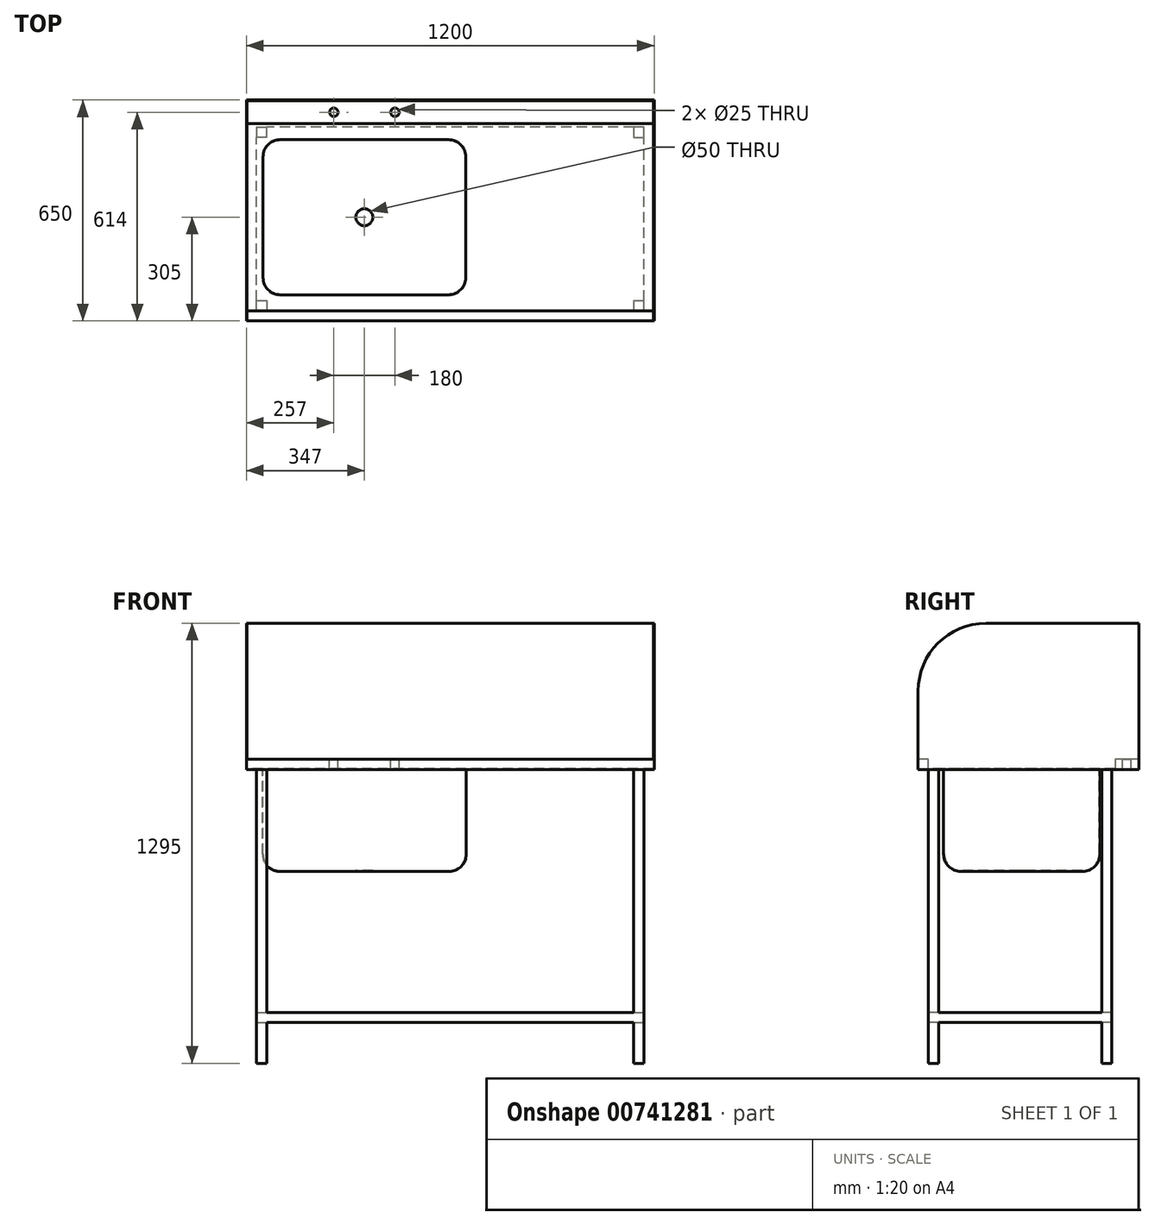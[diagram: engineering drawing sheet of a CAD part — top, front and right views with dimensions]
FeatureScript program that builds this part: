
annotation { "Feature Type Name" : "Feature", "Feature Type Description" : "" }
export const myFeature = defineFeature(function(context is Context, id is Id, definition is map)
    precondition{}
    {
        {
            var Q0;
            Q0=qCreatedBy(makeId("Right.planeOp"),FACE);
            var sketch = newSketch(context, id + "F0", { "sketchPlane" : qUnion([Q0])});
            skLineSegment(sketch, "E0", {"start": v(0, 0) * mm, "end": v(0, -30) * mm});
            skLineSegment(sketch, "E1", {"start": v(0, -30) * mm, "end": v(650, -30) * mm});
            skLineSegment(sketch, "E2", {"start": v(650, -30) * mm, "end": v(650, 400) * mm});
            skLineSegment(sketch, "E3", {"start": v(650, 400) * mm, "end": v(648, 400) * mm});
            skLineSegment(sketch, "E4", {"start": v(648, 400) * mm, "end": v(648, 0) * mm});
            skLineSegment(sketch, "E5", {"start": v(648, 0) * mm, "end": v(580, 0) * mm});
            skLineSegment(sketch, "E6", {"start": v(580, 0) * mm, "end": v(580, -28) * mm});
            skLineSegment(sketch, "E7", {"start": v(580, -28) * mm, "end": v(30, -28) * mm});
            skLineSegment(sketch, "E8", {"start": v(30, -28) * mm, "end": v(30, 0) * mm});
            skLineSegment(sketch, "E9", {"start": v(30, 0) * mm, "end": v(0, 0) * mm});
            skSolve(sketch);
        }
        {
            var Q0;
            Q0 = qSketchRegion(id + "F0", true);
            extrude(context, id + "F1", {"entities" : qUnion([Q0]), "depth" : 1200 * mm, "offsetDistance" : 25 * mm});
        }
        {
            var Q0;
            Q0=qCreatedBy(makeId("Front.planeOp"),FACE);
            var sketch = newSketch(context, id + "F2", { "sketchPlane" : qUnion([Q0])});
            skLineSegment(sketch, "E10.bottom", {"start": v(0, -30) * mm, "end": v(2, -30) * mm});
            skLineSegment(sketch, "E10.top", {"start": v(0, 400) * mm, "end": v(2, 400) * mm});
            skLineSegment(sketch, "E10.left", {"start": v(0, -30) * mm, "end": v(0, 400) * mm});
            skLineSegment(sketch, "E10.right", {"start": v(2, -30) * mm, "end": v(2, 400) * mm});
            skLineSegment(sketch, "E11.bottom", {"start": v(1200, -30) * mm, "end": v(1198, -30) * mm});
            skLineSegment(sketch, "E11.top", {"start": v(1200, 400) * mm, "end": v(1198, 400) * mm});
            skLineSegment(sketch, "E11.left", {"start": v(1200, -30) * mm, "end": v(1200, 400) * mm});
            skLineSegment(sketch, "E11.right", {"start": v(1198, -30) * mm, "end": v(1198, 400) * mm});
            skSolve(sketch);
        }
        {
            var Q0;
            Q0 = qSketchRegion(id + "F2", true);
            var Q1;
            Q1=makeQuery(id+"F1.opExtrude","SWEPT_FACE",FACE,{"disambiguationData":[OSD([sQuery(id+"F0.wireOp",EDGE,"E4")])]});
            extrude(context, id + "F3", {"entities" : qUnion([Q0]), "operationType" : NewBodyOperationType.ADD, "endBound" : BoundingType.UP_TO_SURFACE, "oppositeDirection" : true, "depth" : 25 * mm, "endBoundEntityFace" : qUnion([Q1]), "offsetDistance" : 25 * mm});
        }
        {
            var Q0;
            Q0=makeQuery(id+"F3.opExtrude","CAP_EDGE",EDGE,{"disambiguationData":[OSD([sQuery(id+"F2.wireOp",EDGE,"E10.top")])],"isStart":true});
            var Q1;
            Q1=makeQuery(id+"F3.opExtrude","CAP_EDGE",EDGE,{"disambiguationData":[OSD([sQuery(id+"F2.wireOp",EDGE,"E11.top")])],"isStart":true});
            fillet(context, id + "F4", {"entities" : qUnion([Q0, Q1]), "radius" : 200 * mm, "tangentPropagation" : true, "allowEdgeOverflow" : false});
        }
        {
            var Q0;
            Q0=makeQuery(id+"F1.opExtrude","SWEPT_FACE",FACE,{"disambiguationData":[OSD([sQuery(id+"F0.wireOp",EDGE,"E1")])]});
            var sketch = newSketch(context, id + "F5", { "sketchPlane" : qUnion([Q0])});
            skLineSegment(sketch, "E12.bottom", {"start": v(47, -75) * mm, "end": v(647, -75) * mm});
            skLineSegment(sketch, "E12.top", {"start": v(47, -535) * mm, "end": v(647, -535) * mm});
            skLineSegment(sketch, "E12.left", {"start": v(47, -75) * mm, "end": v(47, -535) * mm});
            skLineSegment(sketch, "E12.right", {"start": v(647, -75) * mm, "end": v(647, -535) * mm});
            skSolve(sketch);
        }
        {
            var Q0;
            Q0 = qSketchRegion(id + "F5", true);
            extrude(context, id + "F6", {"entities" : qUnion([Q0]), "operationType" : NewBodyOperationType.ADD, "depth" : 300 * mm, "offsetDistance" : 25 * mm});
        }
        {
            var Q0;
            Q0=makeQuery(id+"F1.opExtrude","SWEPT_FACE",FACE,{"disambiguationData":[OSD([sQuery(id+"F0.wireOp",EDGE,"E7")])]});
            var sketch = newSketch(context, id + "F7", { "sketchPlane" : qUnion([Q0])});
            skLineSegment(sketch, "E13.bottom", {"start": v(49, 533) * mm, "end": v(645, 533) * mm});
            skLineSegment(sketch, "E13.top", {"start": v(49, 77) * mm, "end": v(645, 77) * mm});
            skLineSegment(sketch, "E13.left", {"start": v(49, 533) * mm, "end": v(49, 77) * mm});
            skLineSegment(sketch, "E13.right", {"start": v(645, 533) * mm, "end": v(645, 77) * mm});
            skSolve(sketch);
        }
        {
            var Q0;
            Q0 = qSketchRegion(id + "F7", true);
            extrude(context, id + "F8", {"entities" : qUnion([Q0]), "operationType" : NewBodyOperationType.REMOVE, "oppositeDirection" : true, "depth" : 300 * mm, "offsetDistance" : 25 * mm});
        }
        {
            var Q0;
            Q0=makeQuery(id+"F8.boolean.opBoolean","COPY",EDGE,{"derivedFrom":makeQuery(id+"F8.opExtrude","SWEPT_EDGE",EDGE,{"disambiguationData":[OSD([sQuery(id+"F7.wireOp",EDGE,"E13.bottom"),sQuery(id+"F7.wireOp",EDGE,"E13.right")])]})});
            var Q1;
            Q1=makeQuery(id+"F8.boolean.opBoolean","COPY",EDGE,{"derivedFrom":makeQuery(id+"F8.opExtrude","SWEPT_EDGE",EDGE,{"disambiguationData":[OSD([sQuery(id+"F7.wireOp",EDGE,"E13.bottom"),sQuery(id+"F7.wireOp",EDGE,"E13.left")])]})});
            var Q2;
            Q2=makeQuery(id+"F8.boolean.opBoolean","COPY",EDGE,{"derivedFrom":makeQuery(id+"F8.opExtrude","SWEPT_EDGE",EDGE,{"disambiguationData":[OSD([sQuery(id+"F7.wireOp",EDGE,"E13.top"),sQuery(id+"F7.wireOp",EDGE,"E13.left")])]})});
            var Q3;
            Q3=makeQuery(id+"F8.boolean.opBoolean","COPY",EDGE,{"derivedFrom":makeQuery(id+"F8.opExtrude","SWEPT_EDGE",EDGE,{"disambiguationData":[OSD([sQuery(id+"F7.wireOp",EDGE,"E13.top"),sQuery(id+"F7.wireOp",EDGE,"E13.right")])]})});
            fillet(context, id + "F9", {"entities" : qUnion([Q0, Q1, Q2, Q3]), "radius" : 50 * mm, "tangentPropagation" : true, "allowEdgeOverflow" : false});
        }
        {
            var Q0;
            Q0=makeQuery(id+"F6.opExtrude","SWEPT_EDGE",EDGE,{"disambiguationData":[OSD([sQuery(id+"F5.wireOp",EDGE,"E12.top"),sQuery(id+"F5.wireOp",EDGE,"E12.left")])]});
            var Q1;
            Q1=makeQuery(id+"F6.opExtrude","SWEPT_EDGE",EDGE,{"disambiguationData":[OSD([sQuery(id+"F5.wireOp",EDGE,"E12.bottom"),sQuery(id+"F5.wireOp",EDGE,"E12.left")])]});
            var Q2;
            Q2=makeQuery(id+"F6.opExtrude","SWEPT_EDGE",EDGE,{"disambiguationData":[OSD([sQuery(id+"F5.wireOp",EDGE,"E12.bottom"),sQuery(id+"F5.wireOp",EDGE,"E12.right")])]});
            var Q3;
            Q3=makeQuery(id+"F6.opExtrude","SWEPT_EDGE",EDGE,{"disambiguationData":[OSD([sQuery(id+"F5.wireOp",EDGE,"E12.top"),sQuery(id+"F5.wireOp",EDGE,"E12.right")])]});
            fillet(context, id + "F10", {"entities" : qUnion([Q0, Q1, Q2, Q3]), "radius" : 50 * mm, "tangentPropagation" : true, "allowEdgeOverflow" : false});
        }
        {
            var Q0;
            Q0=makeQuery(id+"F8.boolean.opBoolean","COPY",EDGE,{"derivedFrom":makeQuery(id+"F8.opExtrude","CAP_EDGE",EDGE,{"disambiguationData":[OSD([sQuery(id+"F7.wireOp",EDGE,"E13.bottom")])],"isStart":false})});
            var Q1;
            Q1=makeQuery(id+"F6.opExtrude","CAP_EDGE",EDGE,{"disambiguationData":[OSD([sQuery(id+"F5.wireOp",EDGE,"E12.left")])],"isStart":false});
            fillet(context, id + "F11", {"entities" : qUnion([Q0, Q1]), "radius" : 50 * mm, "tangentPropagation" : true, "allowEdgeOverflow" : false});
        }
        {
            var Q0;
            Q0=makeQuery(id+"F1.opExtrude","SWEPT_FACE",FACE,{"disambiguationData":[OSD([sQuery(id+"F0.wireOp",EDGE,"E5")])]});
            var sketch = newSketch(context, id + "F12", { "sketchPlane" : qUnion([Q0])});
            skCircle(sketch, "E14", {"center": v(257, 614) * mm, "radius": 12.5 * mm});
            skCircle(sketch, "E15", {"center": v(437, 614) * mm, "radius": 12.5 * mm});
            skSolve(sketch);
        }
        {
            var Q0;
            Q0 = qSketchRegion(id + "F12", true);
            extrude(context, id + "F13", {"entities" : qUnion([Q0]), "operationType" : NewBodyOperationType.REMOVE, "endBound" : BoundingType.UP_TO_NEXT, "oppositeDirection" : true, "depth" : 25 * mm, "offsetDistance" : 25 * mm});
        }
        {
            var Q0;
            Q0=makeQuery(id+"F1.opExtrude","SWEPT_FACE",FACE,{"disambiguationData":[OSD([sQuery(id+"F0.wireOp",EDGE,"E1")])]});
            var sketch = newSketch(context, id + "F14", { "sketchPlane" : qUnion([Q0])});
            skLineSegment(sketch, "E16.bottom", {"start": v(60, -30) * mm, "end": v(30, -30) * mm});
            skLineSegment(sketch, "E16.top", {"start": v(60, -60) * mm, "end": v(30, -60) * mm});
            skLineSegment(sketch, "E16.left", {"start": v(60, -30) * mm, "end": v(60, -60) * mm});
            skLineSegment(sketch, "E16.right", {"start": v(30, -30) * mm, "end": v(30, -60) * mm});
            skPoint(sketch, "E16.middle", {"position": v(45, -45) * mm});
            skLineSegment(sketch, "E17.bottom", {"start": v(1170, -30) * mm, "end": v(1140, -30) * mm});
            skLineSegment(sketch, "E17.top", {"start": v(1170, -60) * mm, "end": v(1140, -60) * mm});
            skLineSegment(sketch, "E17.left", {"start": v(1170, -30) * mm, "end": v(1170, -60) * mm});
            skLineSegment(sketch, "E17.right", {"start": v(1140, -30) * mm, "end": v(1140, -60) * mm});
            skPoint(sketch, "E17.middle", {"position": v(1155, -45) * mm});
            skLineSegment(sketch, "E18.bottom", {"start": v(1170, -540) * mm, "end": v(1140, -540) * mm});
            skLineSegment(sketch, "E18.top", {"start": v(1170, -570) * mm, "end": v(1140, -570) * mm});
            skLineSegment(sketch, "E18.left", {"start": v(1170, -540) * mm, "end": v(1170, -570) * mm});
            skLineSegment(sketch, "E18.right", {"start": v(1140, -540) * mm, "end": v(1140, -570) * mm});
            skPoint(sketch, "E18.middle", {"position": v(1155, -555) * mm});
            skLineSegment(sketch, "E19.bottom", {"start": v(30, -570) * mm, "end": v(60, -570) * mm});
            skLineSegment(sketch, "E19.top", {"start": v(30, -540) * mm, "end": v(60, -540) * mm});
            skLineSegment(sketch, "E19.left", {"start": v(30, -570) * mm, "end": v(30, -540) * mm});
            skLineSegment(sketch, "E19.right", {"start": v(60, -570) * mm, "end": v(60, -540) * mm});
            skPoint(sketch, "E19.middle", {"position": v(45, -555) * mm});
            skSolve(sketch);
        }
        {
            var Q0;
            Q0 = qSketchRegion(id + "F14", true);
            extrude(context, id + "F15", {"entities" : qUnion([Q0]), "operationType" : NewBodyOperationType.ADD, "depth" : 865 * mm, "offsetDistance" : 25 * mm});
        }
        {
            var Q0;
            Q0=makeQuery(id+"F15.opExtrude","SWEPT_FACE",FACE,{"disambiguationData":[OSD([sQuery(id+"F14.wireOp",EDGE,"E16.left")])]});
            var sketch = newSketch(context, id + "F16", { "sketchPlane" : qUnion([Q0])});
            skLineSegment(sketch, "E20.bottom", {"start": v(30, -745) * mm, "end": v(570, -745) * mm});
            skLineSegment(sketch, "E20.top", {"start": v(30, -775) * mm, "end": v(570, -775) * mm});
            skLineSegment(sketch, "E20.left", {"start": v(30, -745) * mm, "end": v(30, -775) * mm});
            skLineSegment(sketch, "E20.right", {"start": v(570, -745) * mm, "end": v(570, -775) * mm});
            skSolve(sketch);
        }
        {
            var Q0;
            Q0 = qSketchRegion(id + "F16", true);
            var Q1;
            Q1=makeQuery(id+"F15.opExtrude","SWEPT_FACE",FACE,{"disambiguationData":[OSD([sQuery(id+"F14.wireOp",EDGE,"E17.left")])]});
            var Q2;
            Q2=makeQuery(id+"F15.opExtrude","SWEPT_FACE",FACE,{"disambiguationData":[OSD([sQuery(id+"F14.wireOp",EDGE,"E16.right")])]});
            extrude(context, id + "F17", {"entities" : qUnion([Q0]), "operationType" : NewBodyOperationType.ADD, "endBound" : BoundingType.UP_TO_SURFACE, "depth" : 25 * mm, "endBoundEntityFace" : qUnion([Q1]), "offsetDistance" : 25 * mm, "hasSecondDirection" : true, "secondDirectionBound" : SecondDirectionBoundingType.UP_TO_SURFACE, "secondDirectionOppositeDirection" : true, "secondDirectionDepth" : 25 * mm, "secondDirectionBoundEntityFace" : qUnion([Q2])});
        }
        {
            var Q0;
            Q0=makeQuery(id+"F8.boolean.opBoolean","COPY",FACE,{"derivedFrom":makeQuery(id+"F8.opExtrude","CAP_FACE",FACE,{"disambiguationData":[OSD([sQuery(id+"F7.wireOp",EDGE,"E13.bottom"),sQuery(id+"F7.wireOp",EDGE,"E13.top"),sQuery(id+"F7.wireOp",EDGE,"E13.left"),sQuery(id+"F7.wireOp",EDGE,"E13.right")])],"isStart":false})});
            var sketch = newSketch(context, id + "F18", { "sketchPlane" : qUnion([Q0])});
            skCircle(sketch, "E21", {"center": v(347, 305) * mm, "radius": 25 * mm});
            skPoint(sketch, "E21.centerSnap0", {"position": v(99, 305) * mm});
            skPoint(sketch, "E21.centerSnap1", {"position": v(347, 483) * mm});
            skSolve(sketch);
        }
        {
            var Q0;
            Q0 = qSketchRegion(id + "F18", true);
            extrude(context, id + "F19", {"entities" : qUnion([Q0]), "operationType" : NewBodyOperationType.REMOVE, "endBound" : BoundingType.UP_TO_NEXT, "oppositeDirection" : true, "depth" : 25 * mm, "offsetDistance" : 25 * mm});
        }
    });
